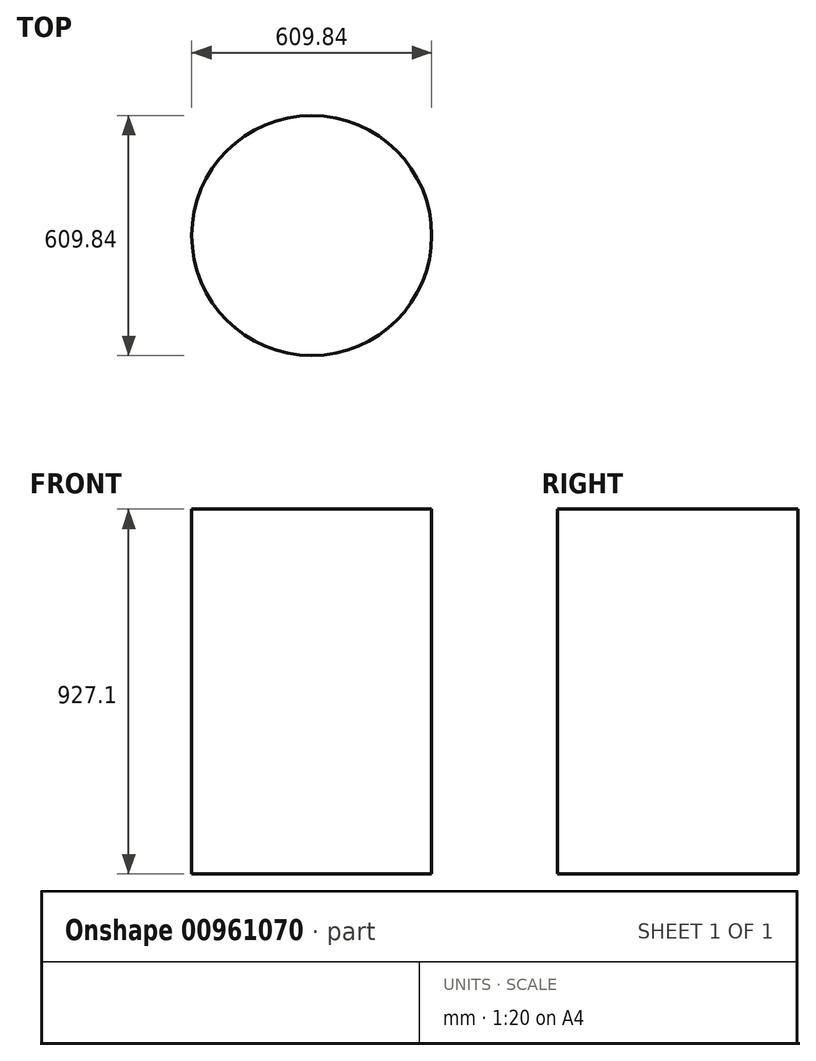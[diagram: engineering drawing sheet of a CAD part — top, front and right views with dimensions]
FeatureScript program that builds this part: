
annotation { "Feature Type Name" : "Feature", "Feature Type Description" : "" }
export const myFeature = defineFeature(function(context is Context, id is Id, definition is map)
    precondition{}
    {
        {
            var Q0;
            Q0=qCreatedBy(makeId("Top.planeOp"),FACE);
            var sketch = newSketch(context, id + "F0", { "sketchPlane" : qUnion([Q0])});
            skCircle(sketch, "E0", {"center": v(0, 0) * mm, "radius": 304.92 * mm});
            skSolve(sketch);
        }
        {
            var Q0;
            Q0=makeQuery(id+"F0.imprint","IMPRINT",FACE,{"disambiguationData":[TD([[makeQuery(id+"F0.imprint","IMPRINT",EDGE,{"derivedFrom":sQuery(id+"F0.wireOp",EDGE,"E0")}),1.0]])]});
            var Q1;
            Q1=sQuery(id+"F0.wireOp",EDGE,"E0");
            extrude(context, id + "F1", {"entities" : qUnion([Q0]), "surfaceEntities" : qUnion([Q1]), "depth" : 927.1 * mm, "offsetDistance" : 25.4 * mm});
        }
    });
